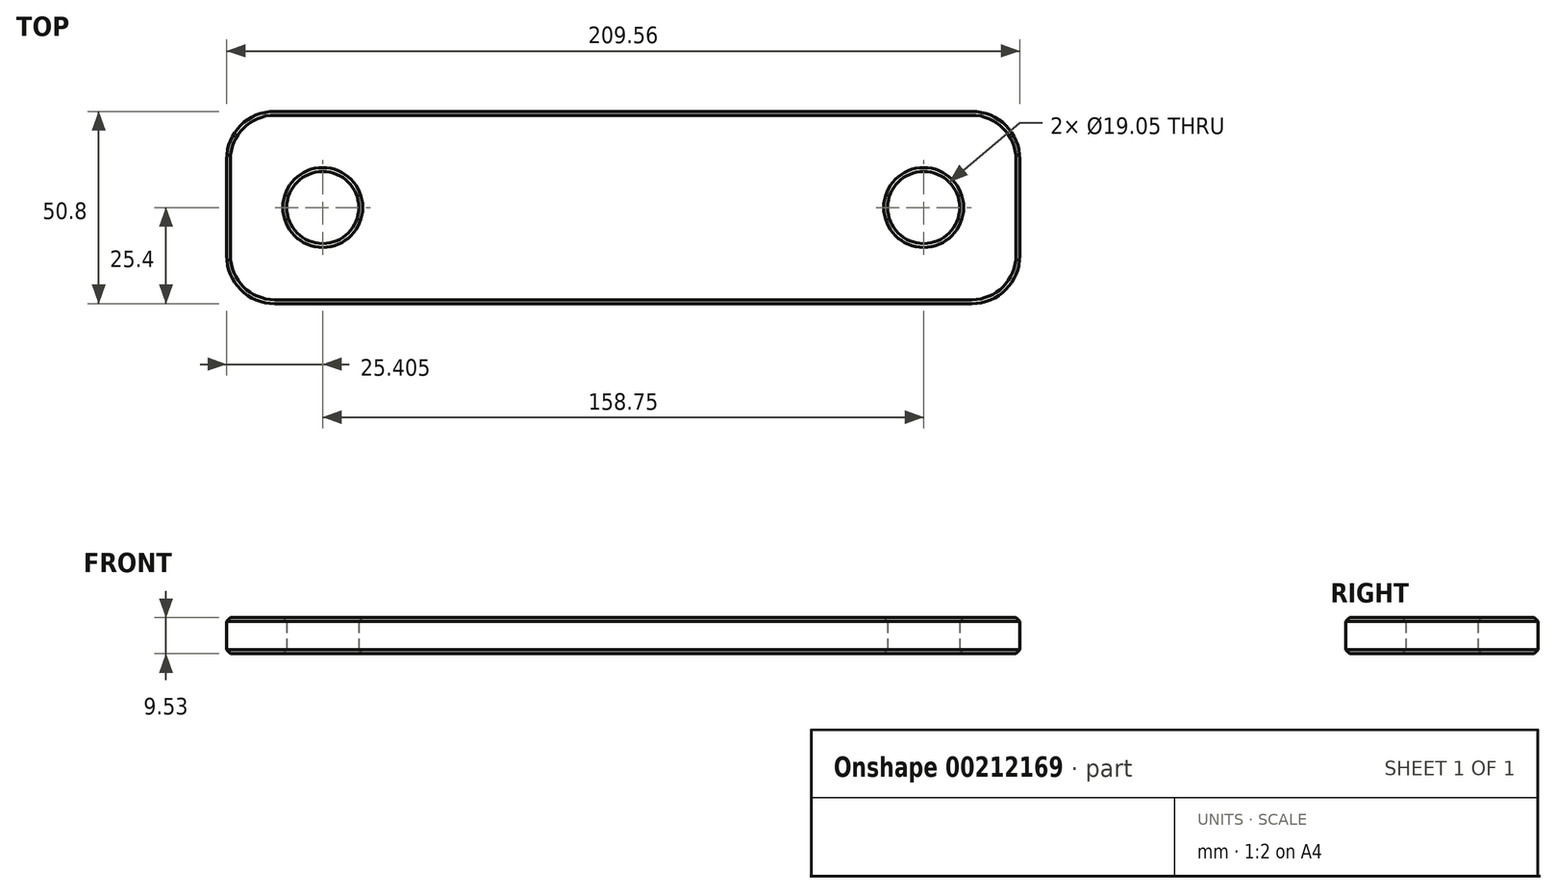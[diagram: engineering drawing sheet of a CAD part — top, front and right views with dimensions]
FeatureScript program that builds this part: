
annotation { "Feature Type Name" : "Feature", "Feature Type Description" : "" }
export const myFeature = defineFeature(function(context is Context, id is Id, definition is map)
    precondition{}
    {
        {
            var Q0;
            Q0=qCreatedBy(makeId("Top.planeOp"),FACE);
            var sketch = newSketch(context, id + "F0", { "sketchPlane" : qUnion([Q0])});
            skLineSegment(sketch, "E0.bottom", {"start": v(-92.08, 25.4) * mm, "end": v(92.08, 25.4) * mm});
            skLineSegment(sketch, "E0.top", {"start": v(-92.08, -25.4) * mm, "end": v(92.08, -25.4) * mm});
            skLineSegment(sketch, "E0.left", {"start": v(-104.78, 12.7) * mm, "end": v(-104.78, -12.7) * mm});
            skLineSegment(sketch, "E0.right", {"start": v(104.78, 12.7) * mm, "end": v(104.78, -12.7) * mm});
            skPoint(sketch, "E0.middle", {"position": v(0, 0) * mm});
            skCircle(sketch, "E1", {"center": v(-79.38, 0) * mm, "radius": 9.53 * mm});
            skCircle(sketch, "E2", {"center": v(79.38, 0) * mm, "radius": 9.53 * mm});
            skLineSegment(sketch, "E3", {"start": v(79.38, 0) * mm, "end": v(0, 0) * mm, "construction": true});
            skLineSegment(sketch, "E4", {"start": v(-79.38, 0) * mm, "end": v(0, 0) * mm, "construction": true});
            skPoint(sketch, "E5.visualSharp", {"position": v(-104.78, 25.4) * mm});
            skArc(sketch, "E5.filletArc", {"start": v(-92.08, 25.4) * mm, "mid": v(-101.06, 21.68) * mm, "end": v(-104.78, 12.7) * mm});
            skPoint(sketch, "E6.visualSharp", {"position": v(-104.78, -25.4) * mm});
            skArc(sketch, "E6.filletArc", {"start": v(-104.77, -12.7) * mm, "mid": v(-101.06, -21.68) * mm, "end": v(-92.08, -25.4) * mm});
            skPoint(sketch, "E7.visualSharp", {"position": v(104.78, -25.4) * mm});
            skArc(sketch, "E7.filletArc", {"start": v(92.08, -25.4) * mm, "mid": v(101.06, -21.68) * mm, "end": v(104.78, -12.7) * mm});
            skPoint(sketch, "E8.visualSharp", {"position": v(104.78, 25.4) * mm});
            skArc(sketch, "E8.filletArc", {"start": v(104.77, 12.7) * mm, "mid": v(101.06, 21.68) * mm, "end": v(92.08, 25.4) * mm});
            skSolve(sketch);
        }
        {
            var Q0;
            Q0=makeQuery(id+"F0.imprint","IMPRINT",FACE,{"disambiguationData":[TD([[makeQuery(id+"F0.imprint","IMPRINT",EDGE,{"derivedFrom":sQuery(id+"F0.wireOp",EDGE,"E0.bottom")}),-1.0]])]});
            extrude(context, id + "F1", {"entities" : qUnion([Q0]), "depth" : 9.52 * mm});
        }
        {
            var Q0;
            Q0=makeQuery(id+"F1.opExtrude","CAP_FACE",FACE,{"disambiguationData":[OSD([sQuery(id+"F0.wireOp",EDGE,"E0.bottom"),sQuery(id+"F0.wireOp",EDGE,"E0.top"),sQuery(id+"F0.wireOp",EDGE,"E0.left"),sQuery(id+"F0.wireOp",EDGE,"E0.right"),sQuery(id+"F0.wireOp",EDGE,"E1"),sQuery(id+"F0.wireOp",EDGE,"E2"),sQuery(id+"F0.wireOp",EDGE,"E5.filletArc"),sQuery(id+"F0.wireOp",EDGE,"E6.filletArc"),sQuery(id+"F0.wireOp",EDGE,"E7.filletArc"),sQuery(id+"F0.wireOp",EDGE,"E8.filletArc")])],"isStart":false});
            var Q1;
            Q1=makeQuery(id+"F1.opExtrude","CAP_FACE",FACE,{"disambiguationData":[OSD([sQuery(id+"F0.wireOp",EDGE,"E0.bottom"),sQuery(id+"F0.wireOp",EDGE,"E0.top"),sQuery(id+"F0.wireOp",EDGE,"E0.left"),sQuery(id+"F0.wireOp",EDGE,"E0.right"),sQuery(id+"F0.wireOp",EDGE,"E1"),sQuery(id+"F0.wireOp",EDGE,"E2"),sQuery(id+"F0.wireOp",EDGE,"E5.filletArc"),sQuery(id+"F0.wireOp",EDGE,"E6.filletArc"),sQuery(id+"F0.wireOp",EDGE,"E7.filletArc"),sQuery(id+"F0.wireOp",EDGE,"E8.filletArc")])],"isStart":true});
            chamfer(context, id + "F2", {"entities" : qUnion([Q0, Q1]), "width" : 1.02 * mm, "tangentPropagation" : true});
        }
    });
